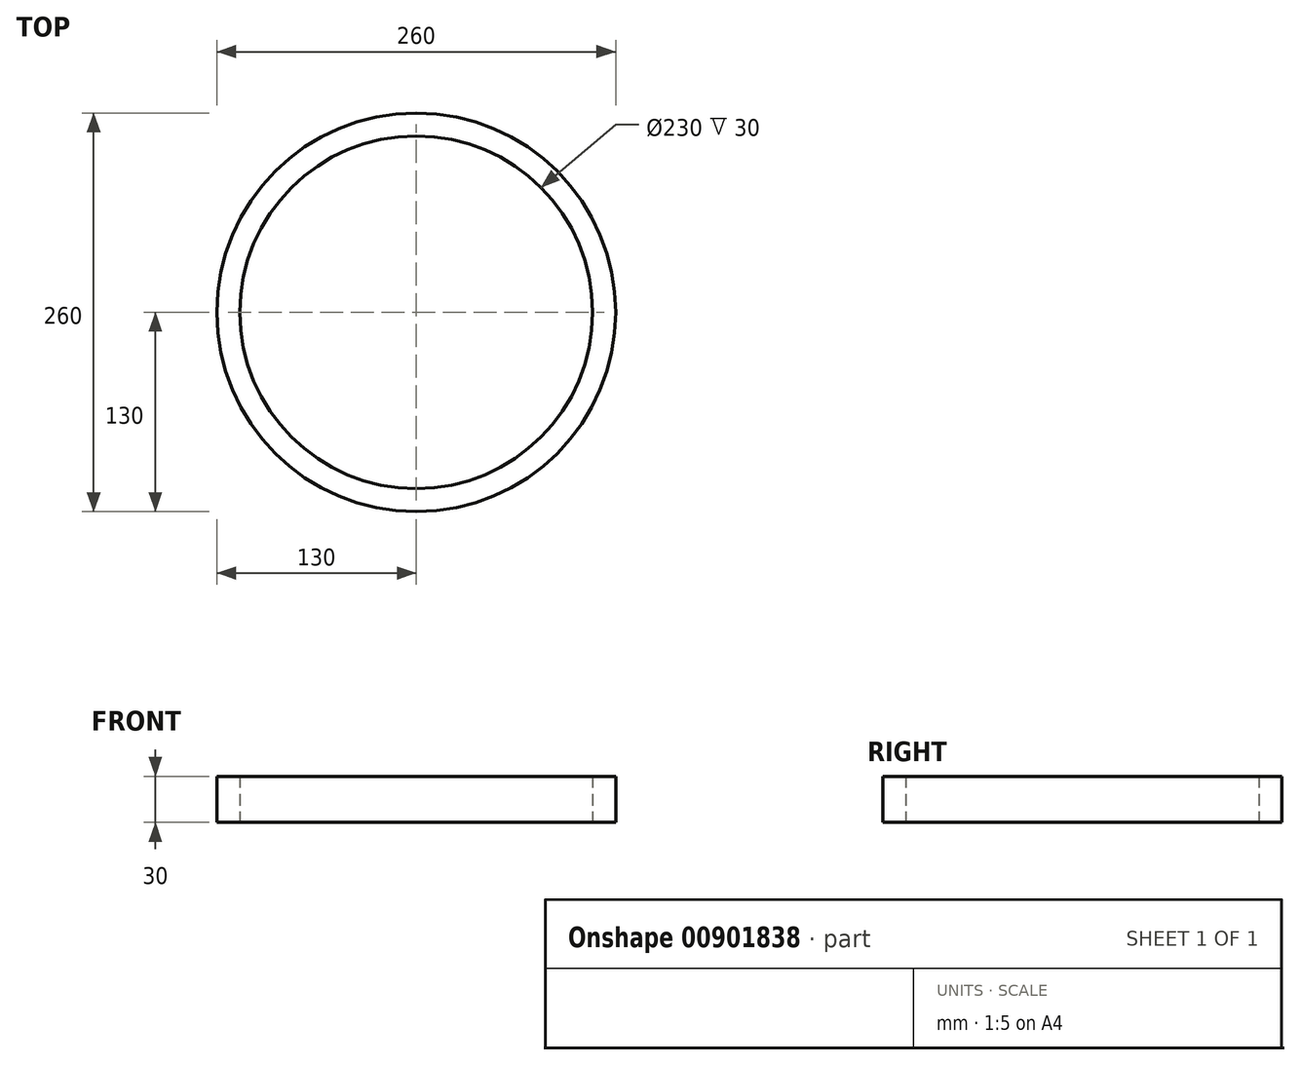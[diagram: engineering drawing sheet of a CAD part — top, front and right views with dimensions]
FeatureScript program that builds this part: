
annotation { "Feature Type Name" : "Feature", "Feature Type Description" : "" }
export const myFeature = defineFeature(function(context is Context, id is Id, definition is map)
    precondition{}
    {
        {
            var Q0;
            Q0=qCreatedBy(makeId("Top.planeOp"),FACE);
            var sketch = newSketch(context, id + "F0", { "sketchPlane" : qUnion([Q0])});
            skCircle(sketch, "E0", {"center": v(0, 0) * mm, "radius": 115 * mm});
            skCircle(sketch, "E1", {"center": v(0, 0) * mm, "radius": 130 * mm});
            skSolve(sketch);
        }
        {
            var Q0;
            Q0=makeQuery(id+"F0.imprint","IMPRINT",FACE,{"disambiguationData":[TD([[makeQuery(id+"F0.imprint","IMPRINT",EDGE,{"derivedFrom":sQuery(id+"F0.wireOp",EDGE,"E0")}),-1.0]])]});
            extrude(context, id + "F1", {"entities" : qUnion([Q0]), "depth" : 30 * mm, "offsetDistance" : 25 * mm});
        }
    });
